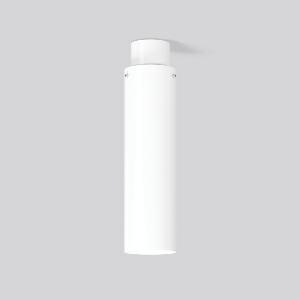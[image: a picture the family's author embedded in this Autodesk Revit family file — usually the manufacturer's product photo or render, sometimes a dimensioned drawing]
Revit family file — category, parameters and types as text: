
# Revit family: glasdownlight_931176_002_1_0701
name_source: partatom
category: Lighting Fixtures
units: mm (PartAtom-declared; Revit-internal decimal feet)

## family parameters
Cut with Voids When Loaded = No
Host = Face
Light Source = No
Part Type = Normal
Room Calculation Point = No
Round Connector Dimension = Use Diameter
Shared = No

## types (1)
- GLASDOWNLIGHT (1 x LED Modul 840, 2500 lm, 4000)
    Apparent Load = 19 VA
    CIE Flux Codes = 16 41 69 51 100
    Color Rendering = 80
    Color Temperature = 4000
    Default Elevation = 1800 mm
    Description = Series: GLASDOWNLIGHT
Decorative round surface-mounted luminaire. Base: aluminium, powder-coated. Mouth blown 3-layer opal glass (Triplex glass) with satin finish. Glass fastening: retaining screws. Triplex glass produces particularly homogeneous, soft and glare free lighting. 
Colour: white
Diameter: 120 mm
Height: 470 mm
Lamp: LED
Socket: without socket
Colour temperature: 4000K
Colour rendering index (CRI): 80
System power: 19 W
Rated luminous flux: 2500 lm
Luminous efficiency: 132 lm/W
Control gear: Regulated power supply
Protection class: I
Type of protection: IP 20
    Height = 470 mm
    Lamp = 1 x LED Modul 840
    Lamp Light Flux = 2500 lm
    Lamp count = 1
    Length = 120 mm
    Lifetime = 50000 h
    Luminous efficacy = 132 lm/W
    Manufacturer = RZB
    ModVariant = No
    Model = 931176.002.1
    Mounting Place = Ceiling
    Mounting Type = Surface mounted
    Number of Poles = 1
    OnlyDefault = Yes
    Power Factor = 1
    Product Name = GLASDOWNLIGHT
    Product group = Surface mounted ceiling luminaires
    ProductGroupID = 303
    Protection Class = Protection class I
    Protection Degree = IP 20
    RLX_Detail_Level = 1
    RLX_Emergency_Light_Flux = 0 lm
    RLX_Emergency_Type = 0
    RLX_Emergency_Type_DB = No
    RlxData = <blob elided: 14333 chars, md5=feaba01f>
    Socket = socket
    Standby Power = 0 W
    System Light Flux = 2500 lm
    System Power = 19 W
    Type Comments = Product without accessories
    Type Image = 931176.002.jpg
    URL = http://relux.com
    VarID = ---
    Voltage = 230 V
    Voltage Range = 220-240 V
    Weight = 0.00 kg
    Width = 0 mm  [stored 0 ft]

note: [stored X ft] marks values corroborated as IEEE doubles in the binary element streams (Revit-internal decimal feet)

## geometry (parser evidence)
native form markers: Sweep x14
no freeform markers — native parametric forms only
